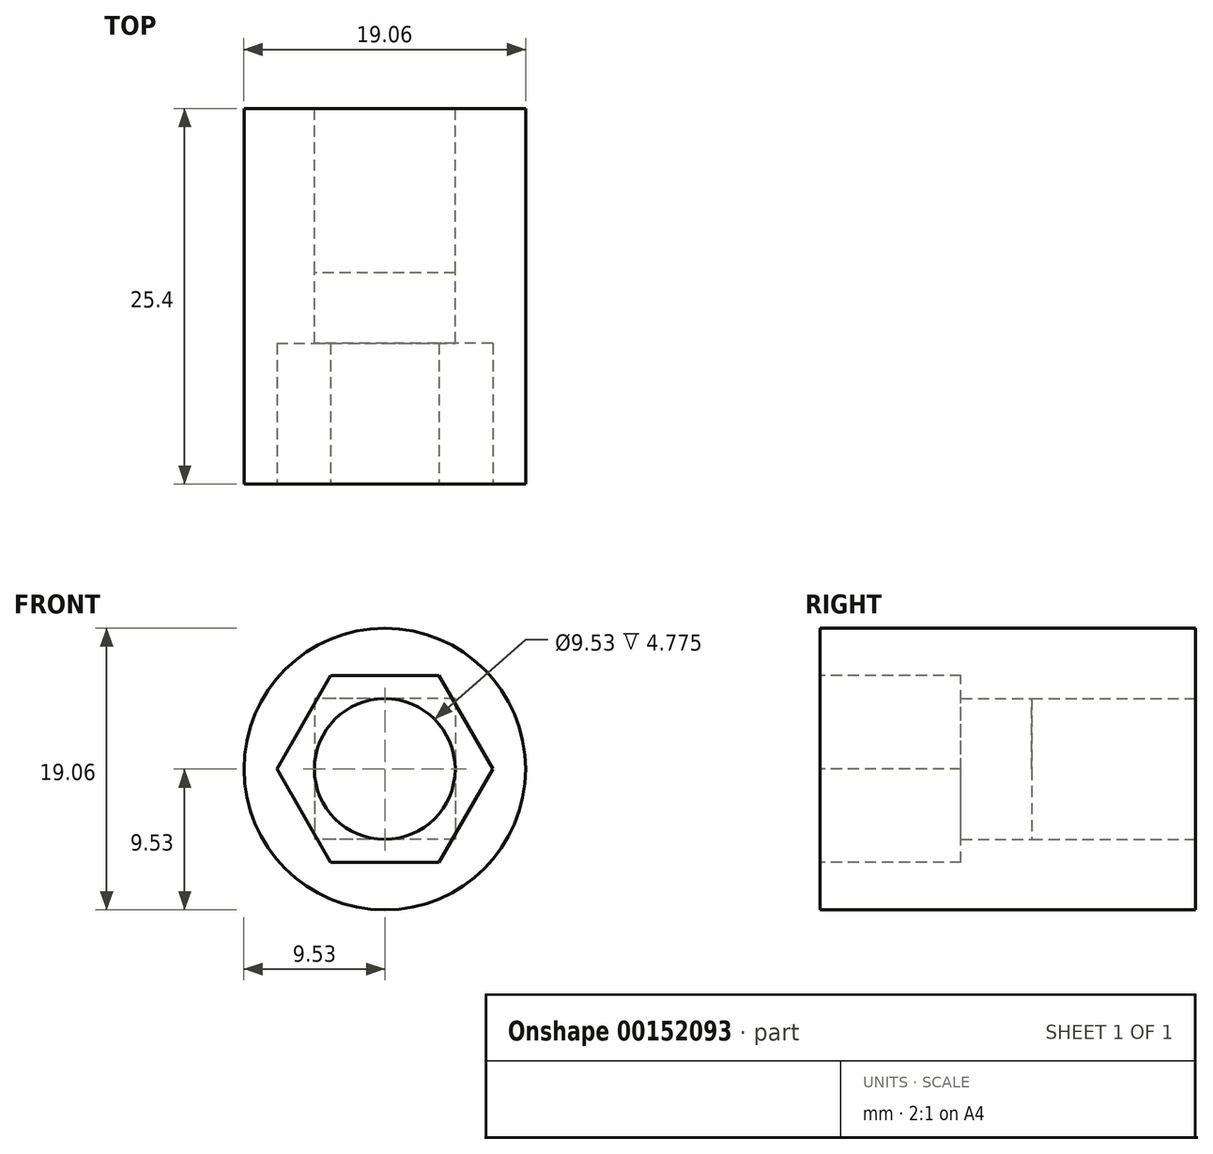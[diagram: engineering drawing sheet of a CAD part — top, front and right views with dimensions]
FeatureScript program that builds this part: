
annotation { "Feature Type Name" : "Feature", "Feature Type Description" : "" }
export const myFeature = defineFeature(function(context is Context, id is Id, definition is map)
    precondition{}
    {
        {
            var Q0;
            Q0=qCreatedBy(makeId("Front.planeOp"),FACE);
            var sketch = newSketch(context, id + "F0", { "sketchPlane" : qUnion([Q0])});
            skCircle(sketch, "E0", {"center": v(0, 0) * mm, "radius": 9.53 * mm});
            skSolve(sketch);
        }
        {
            var Q0;
            Q0=makeQuery(id+"F0.imprint","IMPRINT",FACE,{"disambiguationData":[TD([[makeQuery(id+"F0.imprint","IMPRINT",EDGE,{"derivedFrom":sQuery(id+"F0.wireOp",EDGE,"E0")}),1.0]])]});
            extrude(context, id + "F1", {"entities" : qUnion([Q0]), "depth" : 25.4 * mm});
        }
        {
            var Q0;
            Q0=qCreatedBy(makeId("Front.planeOp"),FACE);
            var sketch = newSketch(context, id + "F2", { "sketchPlane" : qUnion([Q0])});
            skLineSegment(sketch, "E1.bottom", {"start": v(4.76, 4.76) * mm, "end": v(-4.76, 4.76) * mm});
            skLineSegment(sketch, "E1.top", {"start": v(4.76, -4.76) * mm, "end": v(-4.76, -4.76) * mm});
            skLineSegment(sketch, "E1.left", {"start": v(4.76, 4.76) * mm, "end": v(4.76, -4.76) * mm});
            skLineSegment(sketch, "E1.right", {"start": v(-4.76, 4.76) * mm, "end": v(-4.76, -4.76) * mm});
            skPoint(sketch, "E1.middle", {"position": v(0, 0) * mm});
            skCircle(sketch, "E2", {"center": v(0, 0) * mm, "radius": 4.76 * mm});
            skSolve(sketch);
        }
        {
            var Q0;
            {var subQ0=sQuery(id+"F2.wireOp",EDGE,"E2");var subQ1=makeQuery(id+"F2.imprint","INTERSECT",VERTEX,{"derivedFrom":[sQuery(id+"F2.wireOp",EDGE,"E1.bottom"),subQ0]});Q0=makeQuery(id+"F2.imprint","IMPRINT",FACE,{"disambiguationData":[TD([[makeQuery(id+"F2.imprint","IMPRINT",EDGE,{"disambiguationData":[TD([[subQ1,1.0]])],"derivedFrom":subQ0}),1.0]])]});}
            extrude(context, id + "F3", {"entities" : qUnion([Q0]), "operationType" : NewBodyOperationType.REMOVE, "endBound" : BoundingType.THROUGH_ALL, "depth" : 25.4 * mm});
        }
        {
            var Q0;
            Q0 = qSketchRegion(id + "F2", true);
            extrude(context, id + "F4", {"entities" : qUnion([Q0]), "operationType" : NewBodyOperationType.REMOVE, "depth" : 11.1 * mm});
        }
        {
            var Q0;
            Q0=makeQuery(id+"F1.opExtrude","CAP_FACE",FACE,{"disambiguationData":[OSD([sQuery(id+"F0.wireOp",EDGE,"E0")])],"isStart":false});
            var sketch = newSketch(context, id + "F5", { "sketchPlane" : qUnion([Q0])});
            skCircle(sketch, "E3.cCircle", {"center": v(0, 0) * mm, "radius": 6.32 * mm, "construction": true});
            skLineSegment(sketch, "E3.0", {"start": v(-3.65, 6.32) * mm, "end": v(3.65, 6.32) * mm});
            skLineSegment(sketch, "E3.1", {"start": v(3.65, 6.32) * mm, "end": v(7.3, 0) * mm});
            skLineSegment(sketch, "E3.2", {"start": v(7.3, 0) * mm, "end": v(3.65, -6.32) * mm});
            skLineSegment(sketch, "E3.3", {"start": v(3.65, -6.32) * mm, "end": v(-3.65, -6.32) * mm});
            skLineSegment(sketch, "E3.4", {"start": v(-3.65, -6.32) * mm, "end": v(-7.3, 0) * mm});
            skLineSegment(sketch, "E3.5", {"start": v(-7.3, 0) * mm, "end": v(-3.65, 6.32) * mm});
            skPoint(sketch, "E3.0.midPoint", {"position": v(0, 6.32) * mm});
            skSolve(sketch);
        }
        {
            var Q0;
            Q0=makeQuery(id+"F5.imprint","IMPRINT",FACE,{"disambiguationData":[TD([[makeQuery(id+"F5.imprint","IMPRINT",EDGE,{"derivedFrom":sQuery(id+"F5.wireOp",EDGE,"E3.0")}),-1.0]])]});
            extrude(context, id + "F6", {"entities" : qUnion([Q0]), "operationType" : NewBodyOperationType.REMOVE, "oppositeDirection" : true, "depth" : 9.52 * mm});
        }
    });
